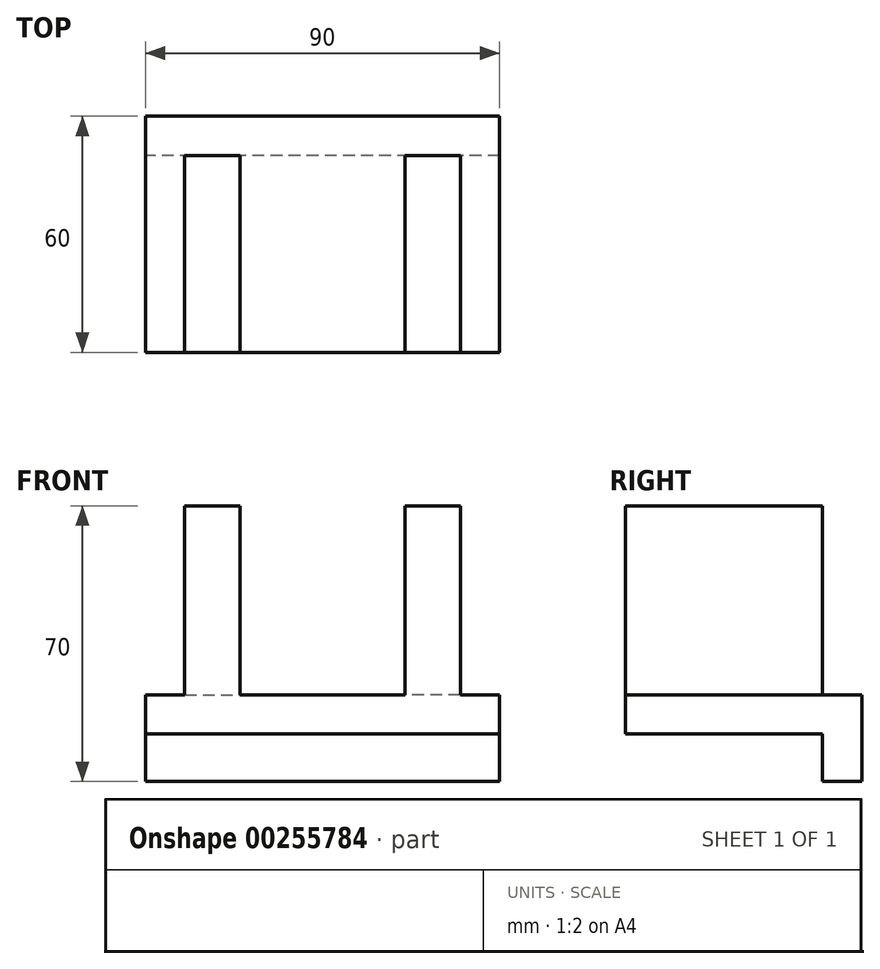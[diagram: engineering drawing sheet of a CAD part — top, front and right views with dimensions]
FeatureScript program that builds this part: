
annotation { "Feature Type Name" : "Feature", "Feature Type Description" : "" }
export const myFeature = defineFeature(function(context is Context, id is Id, definition is map)
    precondition{}
    {
        {
            var Q0;
            Q0=qCreatedBy(makeId("Front.planeOp"),FACE);
            var sketch = newSketch(context, id + "F0", { "sketchPlane" : qUnion([Q0])});
            skLineSegment(sketch, "E0", {"start": v(0, 0) * mm, "end": v(-90, 0) * mm});
            skLineSegment(sketch, "E1", {"start": v(-90, 0) * mm, "end": v(-90, 10) * mm});
            skLineSegment(sketch, "E2", {"start": v(-90, 10) * mm, "end": v(-80, 10) * mm});
            skLineSegment(sketch, "E3", {"start": v(-80, 10) * mm, "end": v(-80, 58) * mm});
            skLineSegment(sketch, "E4", {"start": v(-80, 58) * mm, "end": v(-66, 58) * mm});
            skLineSegment(sketch, "E5", {"start": v(-66, 58) * mm, "end": v(-66, 10) * mm});
            skLineSegment(sketch, "E6", {"start": v(-66, 10) * mm, "end": v(-24, 10) * mm});
            skLineSegment(sketch, "E7", {"start": v(-24, 10) * mm, "end": v(-24, 58) * mm});
            skLineSegment(sketch, "E8", {"start": v(-24, 58) * mm, "end": v(-10, 58) * mm});
            skLineSegment(sketch, "E9", {"start": v(-10, 58) * mm, "end": v(-10, 10) * mm});
            skLineSegment(sketch, "E10", {"start": v(-10, 10) * mm, "end": v(0, 10) * mm});
            skLineSegment(sketch, "E11", {"start": v(0, 10) * mm, "end": v(0, 0) * mm});
            skSolve(sketch);
        }
        {
            var Q0;
            Q0 = qSketchRegion(id + "F0", true);
            extrude(context, id + "F1", {"entities" : qUnion([Q0]), "depth" : 60 * mm});
        }
        {
            var Q0;
            Q0=makeQuery(id+"F1.opExtrude","SWEPT_FACE",FACE,{"disambiguationData":[OSD([sQuery(id+"F0.wireOp",EDGE,"E0")])]});
            var sketch = newSketch(context, id + "F2", { "sketchPlane" : qUnion([Q0])});
            skLineSegment(sketch, "E12", {"start": v(0, 0) * mm, "end": v(0, 10) * mm});
            skLineSegment(sketch, "E13", {"start": v(0, 10) * mm, "end": v(-90, 10) * mm});
            skLineSegment(sketch, "E14", {"start": v(-90, 10) * mm, "end": v(-90, 0) * mm});
            skLineSegment(sketch, "E15", {"start": v(-90, 0) * mm, "end": v(0, 0) * mm});
            skSolve(sketch);
        }
        {
            var Q0;
            Q0 = qSketchRegion(id + "F2", true);
            extrude(context, id + "F3", {"entities" : qUnion([Q0]), "operationType" : NewBodyOperationType.ADD, "depth" : 12 * mm});
        }
        {
            var Q0;
            Q0=makeQuery(id+"F1.opExtrude","SWEPT_FACE",FACE,{"disambiguationData":[OSD([sQuery(id+"F0.wireOp",EDGE,"E8")])]});
            var sketch = newSketch(context, id + "F4", { "sketchPlane" : qUnion([Q0])});
            skLineSegment(sketch, "E16", {"start": v(-10, 0) * mm, "end": v(-10, -10) * mm});
            skLineSegment(sketch, "E17", {"start": v(-10, -10) * mm, "end": v(-24, -10) * mm});
            skLineSegment(sketch, "E18", {"start": v(-24, -10) * mm, "end": v(-24, 0) * mm});
            skLineSegment(sketch, "E19", {"start": v(-24, 0) * mm, "end": v(-10, 0) * mm});
            skSolve(sketch);
        }
        {
            var Q0;
            Q0 = qSketchRegion(id + "F4", true);
            extrude(context, id + "F5", {"entities" : qUnion([Q0]), "operationType" : NewBodyOperationType.REMOVE, "oppositeDirection" : true, "depth" : 48 * mm});
        }
        {
            var Q0;
            Q0=makeQuery(id+"F1.opExtrude","SWEPT_FACE",FACE,{"disambiguationData":[OSD([sQuery(id+"F0.wireOp",EDGE,"E4")])]});
            var sketch = newSketch(context, id + "F6", { "sketchPlane" : qUnion([Q0])});
            skLineSegment(sketch, "E20", {"start": v(-80, 0) * mm, "end": v(-80, -10) * mm});
            skLineSegment(sketch, "E21", {"start": v(-80, -10) * mm, "end": v(-66, -10) * mm});
            skLineSegment(sketch, "E22", {"start": v(-66, -10) * mm, "end": v(-66, 0) * mm});
            skLineSegment(sketch, "E23", {"start": v(-66, 0) * mm, "end": v(-80, 0) * mm});
            skSolve(sketch);
        }
        {
            var Q0;
            Q0 = qSketchRegion(id + "F6", true);
            extrude(context, id + "F7", {"entities" : qUnion([Q0]), "operationType" : NewBodyOperationType.REMOVE, "oppositeDirection" : true, "depth" : 48 * mm});
        }
    });
